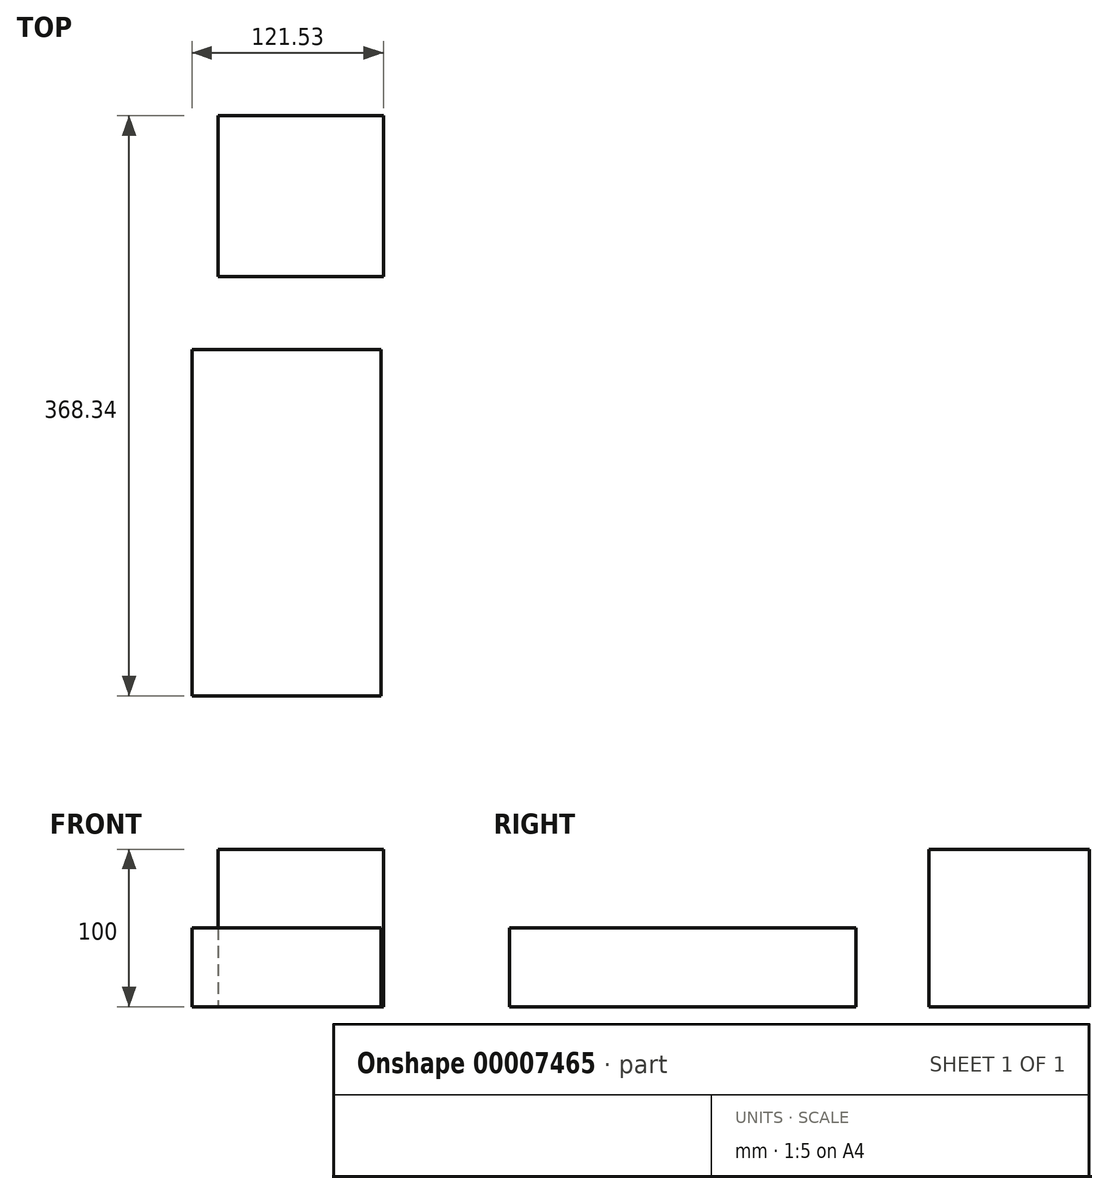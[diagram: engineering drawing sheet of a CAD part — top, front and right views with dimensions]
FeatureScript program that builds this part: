
annotation { "Feature Type Name" : "Feature", "Feature Type Description" : "" }
export const myFeature = defineFeature(function(context is Context, id is Id, definition is map)
    precondition{}
    {
        {
            var Q0;
            Q0=qCreatedBy(makeId("Top.planeOp"),FACE);
            var sketch = newSketch(context, id + "F0", { "sketchPlane" : qUnion([Q0])});
            skLineSegment(sketch, "E0", {"start": v(43.65, 16.56) * mm, "end": v(148.65, 16.56) * mm});
            skLineSegment(sketch, "E1", {"start": v(148.65, 16.56) * mm, "end": v(148.65, 118.56) * mm});
            skLineSegment(sketch, "E2", {"start": v(148.65, 118.56) * mm, "end": v(43.65, 118.56) * mm});
            skLineSegment(sketch, "E3", {"start": v(43.65, 118.56) * mm, "end": v(43.65, 16.56) * mm});
            skSolve(sketch);
        }
        {
            var Q0;
            Q0 = qSketchRegion(id + "F0", true);
            extrude(context, id + "F1", {"entities" : qUnion([Q0]), "depth" : 100 * mm});
        }
        {
            var Q0;
            Q0=qCreatedBy(makeId("Top.planeOp"),FACE);
            var sketch = newSketch(context, id + "F2", { "sketchPlane" : qUnion([Q0])});
            skLineSegment(sketch, "E4.rect.bottom", {"start": v(147.12, -249.78) * mm, "end": v(27.12, -249.78) * mm});
            skLineSegment(sketch, "E4.rect.top", {"start": v(147.12, -29.78) * mm, "end": v(27.12, -29.78) * mm});
            skLineSegment(sketch, "E4.rect.left", {"start": v(147.12, -249.78) * mm, "end": v(147.12, -29.78) * mm});
            skLineSegment(sketch, "E4.rect.right", {"start": v(27.12, -249.78) * mm, "end": v(27.12, -29.78) * mm});
            skPoint(sketch, "E4.rect.middle", {"position": v(87.12, -139.78) * mm});
            skSolve(sketch);
        }
        {
            var Q0;
            Q0 = qSketchRegion(id + "F2", true);
            extrude(context, id + "F3", {"entities" : qUnion([Q0]), "depth" : 50 * mm});
        }
    });
